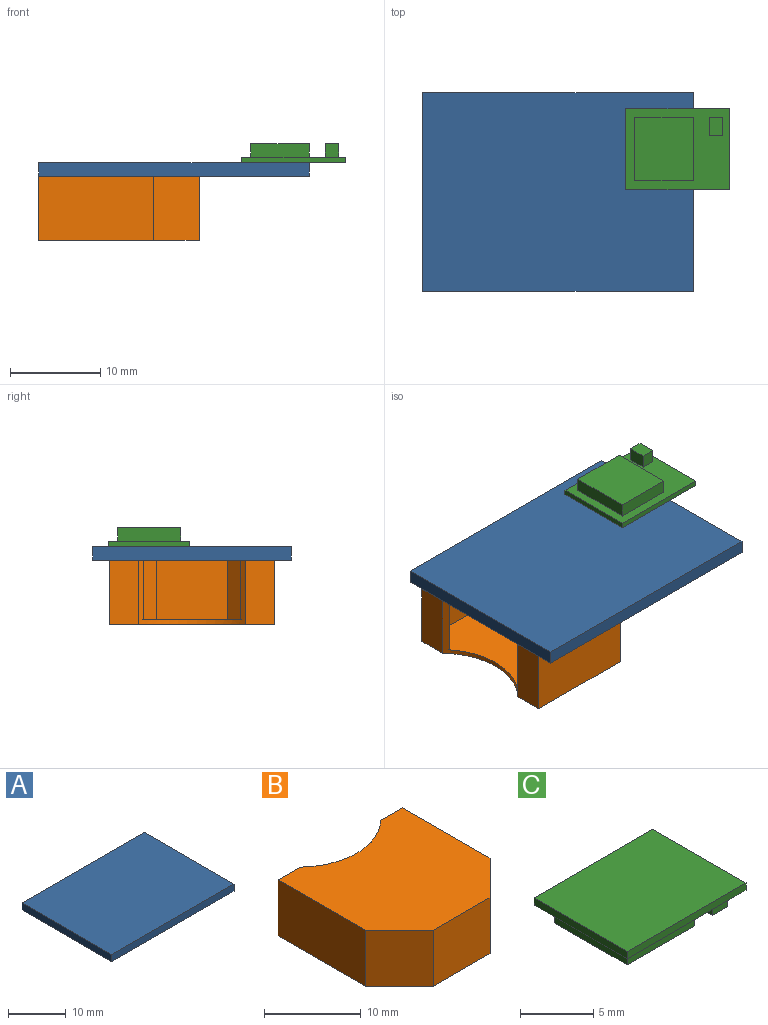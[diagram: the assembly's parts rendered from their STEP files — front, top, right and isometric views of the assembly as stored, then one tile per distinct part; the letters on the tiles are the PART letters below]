
ASSEMBLY  parts=3 mates=4
PART A: 6 faces, bbox 30x22x1.5 mm
  f0: plane 30x1.5mm, normal (0,-1,0), area 45mm2, adj f1,f3,f4,f5
  f1: plane 22x1.5mm, normal (1,0,0), area 33mm2, adj f0,f2,f4,f5
  f2: plane 30x1.5mm, normal (0,1,0), area 45mm2, adj f1,f3,f4,f5
  f3: plane 22x1.5mm, normal (-1,0,0), area 33mm2, adj f0,f2,f4,f5
  f4: plane 30x22mm, normal (0,0,1), area 660mm2, adj f0,f1,f2,f3
  f5: plane 30x22mm, normal (0,0,-1), area 660mm2, adj f0,f1,f2,f3
PART B: 18 faces, bbox 18.3x17.8x7.1 mm
  f0: plane 7.11x3.24mm, normal (0,1,0), area 23mm2, adj f2,f4,f7,f17
  f1: plane 6.61x3.3mm, normal (0,-1,0), area 21.8mm2, adj f2,f11,f14,f17
  f2: plane 18.29x17.78mm, normal (0,0,-1), area 26.6mm2, adj f0,f1,f3,f4,f5,f6,f8,f9
  f3: plane 8.29x7.11mm, normal (0,-1,0), area 58.9mm2, adj f2,f7,f8,f9
  f4: plane 12.78x7.11mm, normal (1,0,0), area 90.9mm2, adj f0,f2,f7,f8
  f5: plane 7.11x3.24mm, normal (0,1,0), area 23mm2, adj f2,f6,f7,f17
  f6: plane 12.78x7.11mm, normal (-1,0,0), area 90.9mm2, adj f2,f5,f7,f9
  f7: plane 18.29x17.78mm, normal (0,0,1), area 280.8mm2, adj f0,f3,f4,f5,f6,f8,f9,f17
  f8: plane 7.11x5mm, normal (0.71,-0.71,0), area 50.3mm2, adj f2,f3,f4,f7
  f9: plane 7.11x5mm, normal (-0.71,-0.71,0), area 50.3mm2, adj f2,f3,f6,f7
  f10: plane 7.88x6.61mm, normal (0,1,0), area 52.1mm2, adj f2,f14,f15,f16
  f11: plane 12.07x6.61mm, normal (-1,0,0), area 79.8mm2, adj f1,f2,f14,f15
  f12: plane 6.61x3.3mm, normal (0,-1,0), area 21.8mm2, adj f2,f13,f14,f17
  f13: plane 12.07x6.61mm, normal (1,0,0), area 79.8mm2, adj f2,f12,f14,f16
  f14: plane 17.29x16.78mm, normal (0,0,-1), area 254.2mm2, adj f1,f10,f11,f12,f13,f15,f16,f17
  f15: plane 6.61x4.71mm, normal (-0.71,0.71,0), area 44mm2, adj f2,f10,f11,f14
  f16: plane 6.61x4.71mm, normal (0.71,0.71,0), area 44mm2, adj f2,f10,f13,f14
  f17: cylinder r=8.5mm len=11.82mm, axis (0,0,1), area 16.5mm2, adj f0,f1,f2,f5,f7,f12,f14
PART C: 16 faces, bbox 11.5x9x2.1 mm
  f0: plane 11.5x9mm, normal (0,0,-1), area 55mm2, adj f1,f2,f3,f4,f6,f7,f8,f9
  f1: plane 11.5x0.6mm, normal (0,-1,0), area 6.9mm2, adj f0,f2,f4,f5
  f2: plane 9x0.6mm, normal (1,0,0), area 5.4mm2, adj f0,f1,f3,f5
  f3: plane 11.5x0.6mm, normal (0,1,0), area 6.9mm2, adj f0,f2,f4,f5
  f4: plane 9x0.6mm, normal (-1,0,0), area 5.4mm2, adj f0,f1,f3,f5
  f5: plane 11.5x9mm, normal (0,0,1), area 103.5mm2, adj f1,f2,f3,f4
  f6: plane 6.5x1.5mm, normal (0,-1,0), area 9.8mm2, adj f0,f7,f8,f10
  f7: plane 7x1.5mm, normal (-1,0,0), area 10.5mm2, adj f0,f6,f9,f10
  f8: plane 7x1.5mm, normal (1,0,0), area 10.5mm2, adj f0,f6,f9,f10
  f9: plane 6.5x1.5mm, normal (0,1,0), area 9.8mm2, adj f0,f7,f8,f10
  f10: plane 7x6.5mm, normal (0,0,-1), area 45.5mm2, adj f6,f7,f8,f9
  f11: plane 1.5x1.5mm, normal (0,-1,0), area 2.3mm2, adj f0,f12,f14,f15
  f12: plane 2x1.5mm, normal (1,0,0), area 3mm2, adj f0,f11,f13,f15
  f13: plane 1.5x1.5mm, normal (0,1,0), area 2.3mm2, adj f0,f12,f14,f15
  f14: plane 2x1.5mm, normal (-1,0,0), area 3mm2, adj f0,f11,f13,f15
  f15: plane 2x1.5mm, normal (0,0,-1), area 3mm2, adj f11,f12,f13,f14
PLACE A at identity fixed
PLACE B rot(axis=(0.71,-0.71,0),180deg) t=(-6.11,0,0)mm
PLACE C rot(axis=(1,0,0),180deg) t=(13.25,4.72,1.8)mm
MATE planar C.f8 <-> A.f1  axis (1,0,0) through (15,4.72,2.85)mm
MATE planar B.f0 <-> A.f3  axis (-1,0,0) through (-15,-7.53,-3.55)mm
MATE planar B.f2 <-> A.f5  axis (0,0,1) through (-5.39,0,0)mm
MATE planar C.f5 <-> A.f4  axis (0,0,-1) through (13.25,4.72,1.5)mm
